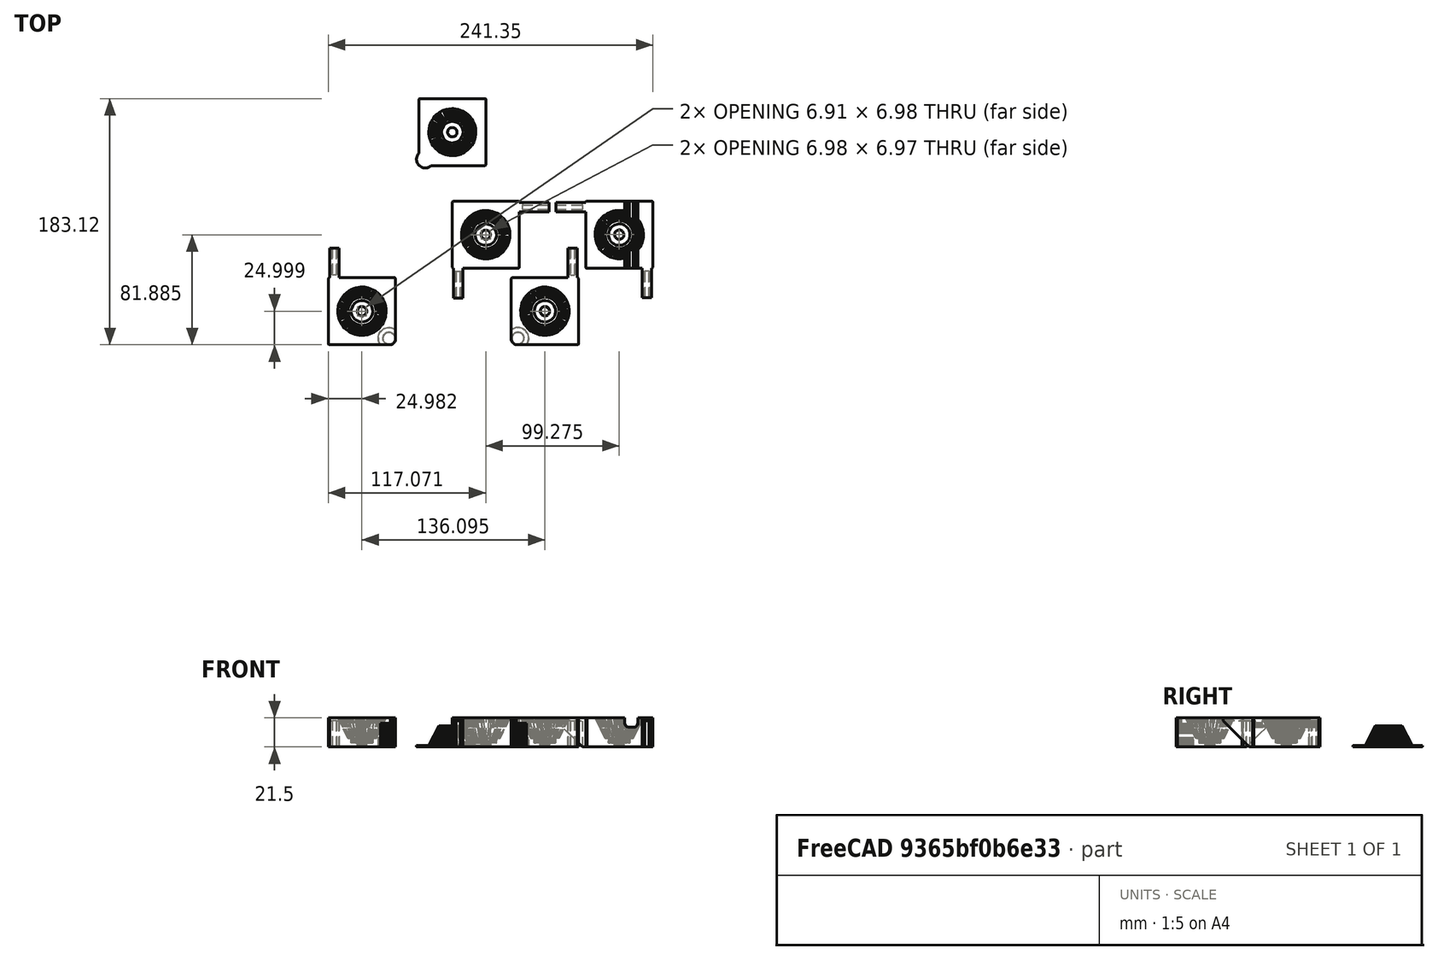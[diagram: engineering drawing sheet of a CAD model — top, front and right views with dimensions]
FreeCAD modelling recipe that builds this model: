
FCSTD DOCUMENT  (FreeCAD 0.18R16146 (Git))
Label: bottom-holder
License: All rights reserved
LicenseURL: http://en.wikipedia.org/wiki/All_rights_reserved
objects: Part::Feature×6, Part::Box×5, Part::Cut×5
note: 16 computed .brp shape members not serialized (recipe doc carries the construction recipe); baked Part::Feature solids carry a one-line shape summary decoded from their .brp

FEATURE [Part::Feature] bottom_mount_handle001001_solid  label="bottom_mount_handle002 (Solid)"
  Placement = pos=(0,57.2,0) rot=(0,0,1;0rad)
  shape: bbox 51.63 x 51.59 x 15.5 mm, 310 faces (baked)
FEATURE [Part::Feature] bottom_corner_plain001001_solid  label="bottom_corner_plain002 (Solid)"
  Placement = pos=(-30.8,30.8,0) rot=(0,0,1;0rad)
  shape: bbox 72 x 72 x 21.5 mm, 280 faces (baked)
FEATURE [Part::Feature] bottom_corner_handle001001_solid  label="bottom_corner_handle002 (Solid)"
  Placement = pos=(0,35.2,0) rot=(0,0,1;0rad)
  shape: bbox 50 x 72 x 21.5 mm, 415 faces (baked)
FEATURE [Part::Feature] bottom_corner_cable_router001001_solid  label="bottom_corner_cable_router002 (Solid)"
  Placement = pos=(-8.8,17.6,0) rot=(0,0,1;0rad)
  shape: bbox 72 x 72 x 21.5 mm, 434 faces (baked)
FEATURE [Part::Box] Box  label="Cube"
  AttacherType = Attacher::AttachEngine3D
  Height = 19.5
  Length = 3.3
  Placement = pos=(-61.61,-15.96,0) rot=(0,0,1;0rad)
  Width = 22
FEATURE [Part::Box] Box001  label="Cube001"
  AttacherType = Attacher::AttachEngine3D
  Height = 19.5
  Length = 3.3
  Placement = pos=(23.38,3.15,0) rot=(0,0,1;0rad)
  Width = 22
FEATURE [Part::Box] Box002  label="Cube002"
  AttacherType = Attacher::AttachEngine3D
  Height = 19.5
  Length = 3.3
  Placement = pos=(78.67,-15.9,0) rot=(0,0,1;0rad)
  Width = 22
FEATURE [Part::Box] Box003  label="Cube003"
  AttacherType = Attacher::AttachEngine3D
  Height = 19.5
  Length = 22
  Placement = pos=(-12.46,51.88,0) rot=(0,0,1;0rad)
  Width = 3.3
FEATURE [Part::Cut] Cut
  Base = -> bottom_corner_plain001001_solid
  Tool = -> Box
FEATURE [Part::Cut] Cut001  label="bottom-handle"
  Base = -> bottom_corner_handle001001_solid
  Tool = -> Box001
FEATURE [Part::Cut] Cut002
  Base = -> bottom_corner_cable_router001001_solid
  Tool = -> Box002
FEATURE [Part::Box] Box004  label="Cube004"
  AttacherType = Attacher::AttachEngine3D
  Height = 19.5
  Length = 22
  Placement = pos=(10.82,51.95,0) rot=(0,0,1;0rad)
  Width = 3.3
FEATURE [Part::Cut] Cut003  label="bottom-wire-route"
  Base = -> Cut002
  Tool = -> Box004
FEATURE [Part::Cut] Cut004  label="nottom-plain"
  Base = -> Cut
  Tool = -> Box003
FEATURE [Part::Feature] Cut001001  label="bottom-handle001"
  shape: bbox 50 x 72 x 21.5 mm, 422 faces (baked)
FEATURE [Part::Feature] Part__Mirroring001  label="bottom-handle001 (Mirror #1)001"
  Placement = pos=(-127,0,0) rot=(0,0,1;0rad)
  shape: bbox 50 x 72 x 21.5 mm, 422 faces (baked)
